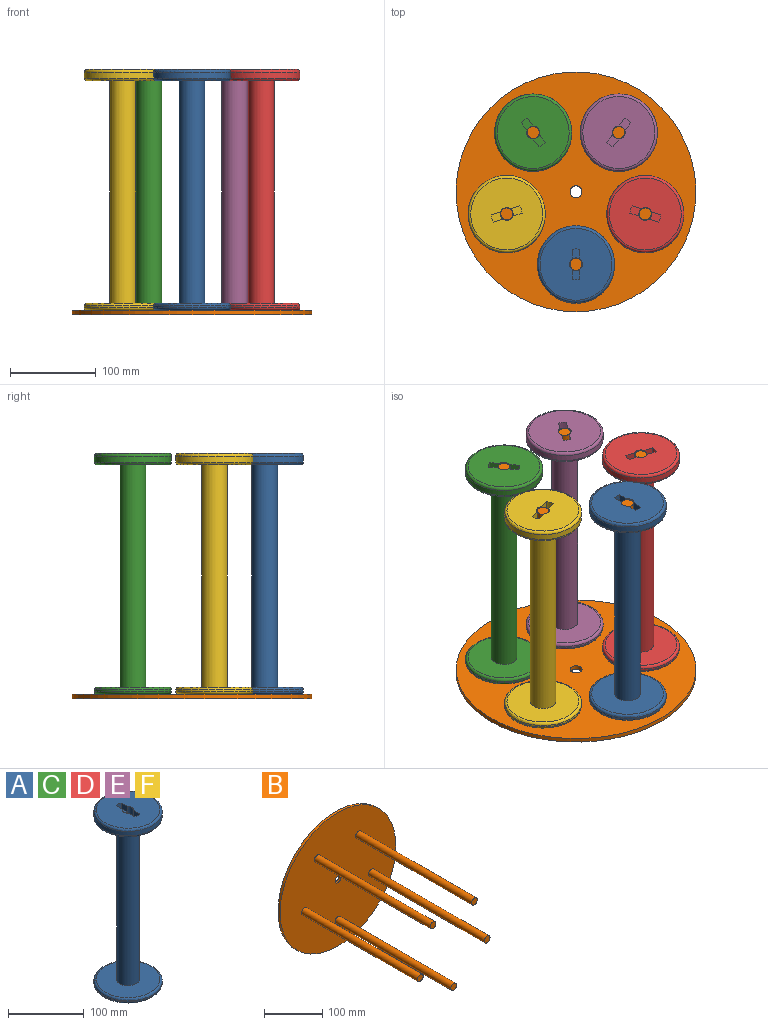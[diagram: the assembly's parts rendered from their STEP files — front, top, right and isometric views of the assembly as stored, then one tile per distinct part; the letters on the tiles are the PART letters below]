
ASSEMBLY  parts=6 mates=1
PART A: 24 faces, bbox 97.4x97.4x281 mm
  f0: cylinder r=7.5mm len=43mm, axis (0,0,1), area 1852.6mm2, adj f1,f8,f16,f18,f19,f21,f22,f23
  f1: plane 84x84mm, normal (0,0,1), area 5169.6mm2, adj f0,f14,f16,f17,f18,f20,f21,f22
  f2: plane 84x84mm, normal (0,0,1), area 4834.9mm2, adj f11,f12
  f3: cylinder r=45mm len=90mm, axis (0,0,1), area 565.5mm2, adj f12,f13
  f4: plane 84x84mm, normal (0,0,-1), area 5365.1mm2, adj f5,f13
  f5: cylinder r=7.5mm len=38mm, axis (0,0,1), area 1790.7mm2, adj f4,f6
  f6: plane 26x26mm, normal (0,0,1), area 354.2mm2, adj f5,f7
  f7: cylinder r=13mm len=200mm, axis (0,0,1), area 16336.3mm2, adj f6,f8
  f8: plane 26x26mm, normal (0,0,-1), area 354.2mm2, adj f0,f7
  f9: cylinder r=45mm len=90mm, axis (0,0,1), area 1979.2mm2, adj f14,f15
  f10: plane 84x84mm, normal (0,0,-1), area 4834.9mm2, adj f11,f15
  f11: cylinder r=15mm len=260mm, axis (0,0,1), area 24504.4mm2, adj f2,f10
  f12: torus R=42mm, axis (0,0,-1), area 1300.1mm2, adj f2,f3
  f13: torus R=42mm, axis (0,0,1), area 1300.1mm2, adj f3,f4
  f14: torus R=42mm, axis (0,0,-1), area 1300.1mm2, adj f1,f9
  f15: torus R=42mm, axis (0,0,1), area 1300.1mm2, adj f9,f10
  f16: plane 11.5x9mm, normal (-1,0,0), area 103.5mm2, adj f0,f1,f17,f19
  f17: cylinder r=18.07mm len=9mm, axis (0,0,1), area 81.9mm2, adj f1,f16,f18,f19
  f18: plane 11.5x9mm, normal (1,0,0), area 103.5mm2, adj f0,f1,f17,f19
  f19: plane 12.07x9mm, normal (0,0,1), area 97.7mm2, adj f0,f16,f17,f18
  f20: cylinder r=18.07mm len=9mm, axis (0,0,1), area 81.9mm2, adj f1,f21,f22,f23
  f21: plane 11.5x9mm, normal (-1,0,0), area 103.5mm2, adj f0,f1,f20,f23
  f22: plane 11.5x9mm, normal (1,0,0), area 103.5mm2, adj f0,f1,f20,f23
  f23: plane 12.07x9mm, normal (0,0,1), area 97.7mm2, adj f0,f20,f21,f22
PART B: 14 faces, bbox 280x285x280 mm
  f0: cylinder r=7mm len=14mm, axis (0,1,0), area 219.9mm2, adj f2,f3
  f1: cylinder r=140mm len=280mm, axis (0,1,0), area 4398.2mm2, adj f2,f3
  f2: plane 280x280mm, normal (0,-1,0), area 60651.6mm2, adj f0,f1,f4,f6,f8,f10,f12
  f3: plane 280x280mm, normal (0,1,0), area 61421.3mm2, adj f0,f1
  f4: cylinder r=7mm len=280mm, axis (0,1,0), area 12315mm2, adj f2,f5
  f5: plane 14x14mm, normal (0,-1,0), area 153.9mm2, adj f4
  f6: cylinder r=7mm len=280mm, axis (0,1,0), area 12315mm2, adj f2,f7
  f7: plane 14x14mm, normal (0,-1,0), area 153.9mm2, adj f6
  f8: cylinder r=7mm len=280mm, axis (0,1,0), area 12315mm2, adj f2,f9
  f9: plane 14x14mm, normal (0,-1,0), area 153.9mm2, adj f8
  f10: cylinder r=7mm len=280mm, axis (0,1,0), area 12315mm2, adj f2,f11
  f11: plane 14x14mm, normal (0,-1,0), area 153.9mm2, adj f10
  f12: cylinder r=7mm len=280mm, axis (0,1,0), area 12315mm2, adj f2,f13
  f13: plane 14x14mm, normal (0,-1,0), area 153.9mm2, adj f12
PART C: same geometry as A
PART D: same geometry as A
PART E: same geometry as A
PART F: same geometry as A
PLACE A t=(0,-85.07,5)mm
PLACE B rot(axis=(-1,0,0),90deg) t=(0,-200,0)mm
PLACE C rot(axis=(0,0,-1),144deg) t=(-50,68.82,5)mm
PLACE D rot(axis=(0,0,1),72deg) t=(80.9,-26.29,5)mm
PLACE E rot(axis=(0,0,1),144deg) t=(50,68.82,5)mm
PLACE F rot(axis=(0,0,-1),72deg) t=(-80.9,-26.29,5)mm
MATE revolute A.f0 <-> B.f10  axis (0,0,-1) through (0,-85.07,5)mm
